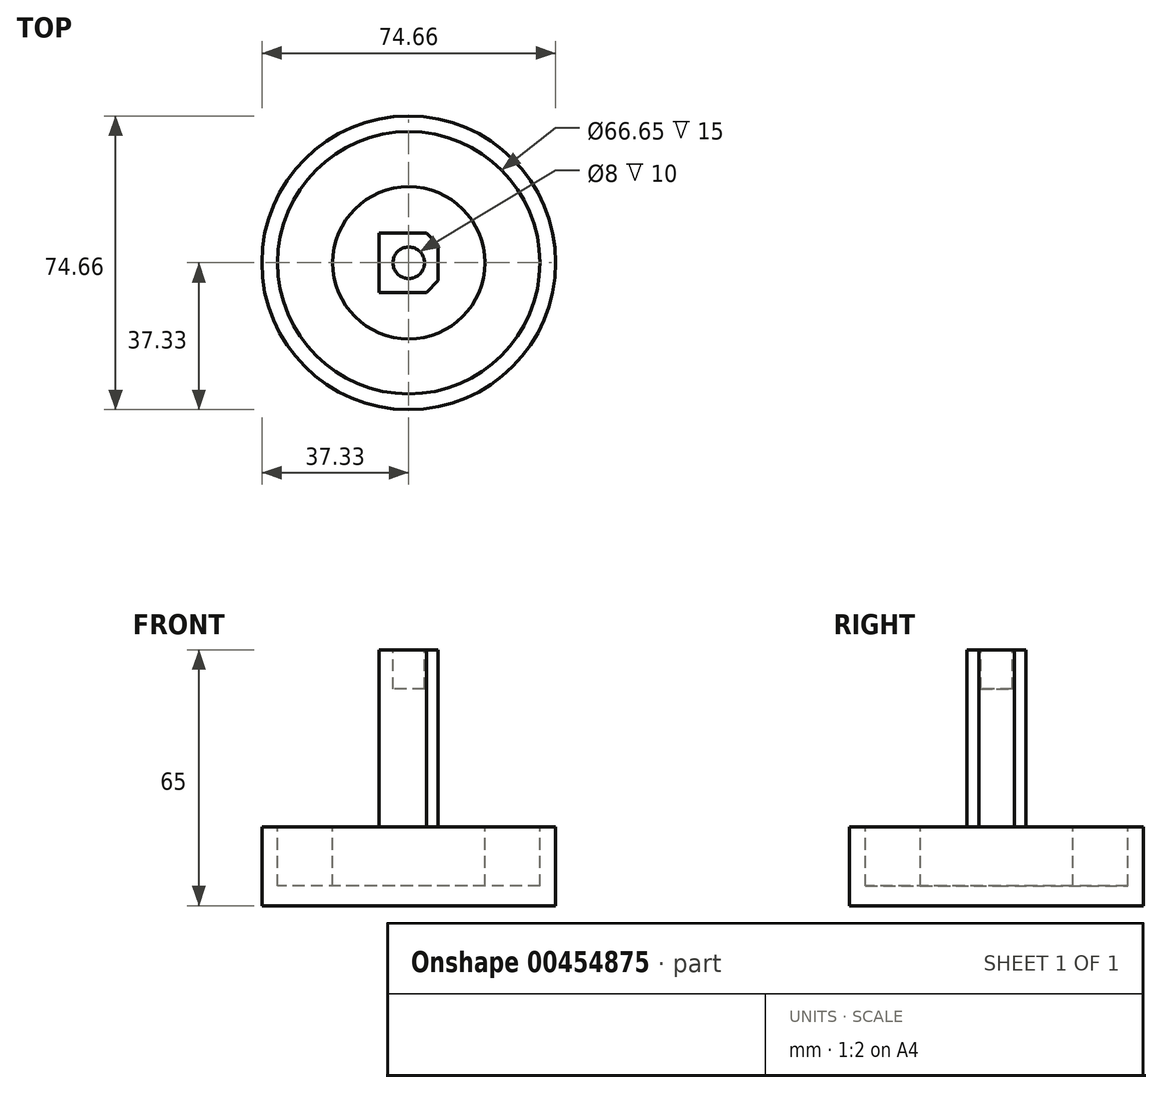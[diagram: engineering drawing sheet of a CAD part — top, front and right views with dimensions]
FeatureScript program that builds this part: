
annotation { "Feature Type Name" : "Feature", "Feature Type Description" : "" }
export const myFeature = defineFeature(function(context is Context, id is Id, definition is map)
    precondition{}
    {
        {
            var Q0;
            Q0=qCreatedBy(makeId("Top.planeOp"),FACE);
            var sketch = newSketch(context, id + "F0", { "sketchPlane" : qUnion([Q0])});
            skCircle(sketch, "E0", {"center": v(0, 0) * mm, "radius": 37.33 * mm});
            skSolve(sketch);
        }
        {
            var Q0;
            Q0=makeQuery(id+"F0.imprint","IMPRINT",FACE,{"disambiguationData":[TD([[makeQuery(id+"F0.imprint","IMPRINT",EDGE,{"derivedFrom":sQuery(id+"F0.wireOp",EDGE,"E0")}),1.0]])]});
            extrude(context, id + "F1", {"entities" : qUnion([Q0]), "depth" : 20 * mm});
        }
        {
            var Q0;
            Q0=makeQuery(id+"F1.opExtrude","CAP_FACE",FACE,{"disambiguationData":[OSD([sQuery(id+"F0.wireOp",EDGE,"E0")])],"isStart":false});
            var sketch = newSketch(context, id + "F2", { "sketchPlane" : qUnion([Q0])});
            skCircle(sketch, "E1.0", {"center": v(0, 0) * mm, "radius": 33.33 * mm});
            skCircle(sketch, "E2.0", {"center": v(0, 0) * mm, "radius": 19.33 * mm});
            skSolve(sketch);
        }
        {
            var Q0;
            Q0=makeQuery(id+"F2.imprint","IMPRINT",FACE,{"disambiguationData":[TD([[makeQuery(id+"F2.imprint","IMPRINT",EDGE,{"derivedFrom":sQuery(id+"F2.wireOp",EDGE,"E1.0")}),1.0]])]});
            extrude(context, id + "F3", {"entities" : qUnion([Q0]), "operationType" : NewBodyOperationType.REMOVE, "oppositeDirection" : true, "depth" : 15 * mm});
        }
        {
            var Q0;
            Q0=makeQuery(id+"F3.boolean.opBoolean","SPLIT",FACE,{"disambiguationData":[TD([makeQuery(id+"F3.opExtrude","SWEPT_FACE",FACE,{"disambiguationData":[OSD([sQuery(id+"F2.wireOp",EDGE,"E2.0")])]})])],"derivedFrom":makeQuery(id+"F1.opExtrude","CAP_FACE",FACE,{"disambiguationData":[OSD([sQuery(id+"F0.wireOp",EDGE,"E0")])],"isStart":false})});
            var sketch = newSketch(context, id + "F4", { "sketchPlane" : qUnion([Q0])});
            skLineSegment(sketch, "E3.bottom", {"start": v(7.5, 7.5) * mm, "end": v(-7.5, 7.5) * mm});
            skLineSegment(sketch, "E3.top", {"start": v(7.5, -7.5) * mm, "end": v(-7.5, -7.5) * mm});
            skLineSegment(sketch, "E3.left", {"start": v(7.5, 7.5) * mm, "end": v(7.5, -7.5) * mm});
            skLineSegment(sketch, "E3.right", {"start": v(-7.5, 7.5) * mm, "end": v(-7.5, -7.5) * mm});
            skPoint(sketch, "E3.middle", {"position": v(0, 0) * mm});
            skSolve(sketch);
        }
        {
            var Q0;
            Q0=makeQuery(id+"F4.imprint","IMPRINT",FACE,{"disambiguationData":[TD([[makeQuery(id+"F4.imprint","IMPRINT",EDGE,{"derivedFrom":sQuery(id+"F4.wireOp",EDGE,"E3.bottom")}),1.0]])]});
            extrude(context, id + "F5", {"entities" : qUnion([Q0]), "operationType" : NewBodyOperationType.ADD, "depth" : 45 * mm});
        }
        {
            var Q0;
            Q0=makeQuery(id+"F5.opExtrude","SWEPT_EDGE",EDGE,{"disambiguationData":[OSD([sQuery(id+"F4.wireOp",EDGE,"E3.bottom"),sQuery(id+"F4.wireOp",EDGE,"E3.left")])]});
            var Q1;
            Q1=makeQuery(id+"F5.opExtrude","SWEPT_EDGE",EDGE,{"disambiguationData":[OSD([sQuery(id+"F4.wireOp",EDGE,"E3.top"),sQuery(id+"F4.wireOp",EDGE,"E3.left")])]});
            chamfer(context, id + "F6", {"entities" : qUnion([Q0, Q1]), "chamferType" : ChamferType.OFFSET_ANGLE, "width" : 3 * mm, "oppositeDirection" : false, "angle" : 45 * degree, "tangentPropagation" : true});
        }
        {
            var Q0;
            Q0=makeQuery(id+"F5.opExtrude","CAP_FACE",FACE,{"disambiguationData":[OSD([sQuery(id+"F4.wireOp",EDGE,"E3.bottom"),sQuery(id+"F4.wireOp",EDGE,"E3.top"),sQuery(id+"F4.wireOp",EDGE,"E3.left"),sQuery(id+"F4.wireOp",EDGE,"E3.right")])],"isStart":false});
            var sketch = newSketch(context, id + "F7", { "sketchPlane" : qUnion([Q0])});
            skCircle(sketch, "E4", {"center": v(0, 0) * mm, "radius": 4 * mm});
            skSolve(sketch);
        }
        {
            var Q0;
            Q0=makeQuery(id+"F7.imprint","IMPRINT",FACE,{"disambiguationData":[TD([[makeQuery(id+"F7.imprint","IMPRINT",EDGE,{"derivedFrom":sQuery(id+"F7.wireOp",EDGE,"E4")}),1.0]])]});
            extrude(context, id + "F8", {"entities" : qUnion([Q0]), "operationType" : NewBodyOperationType.REMOVE, "oppositeDirection" : true, "depth" : 10 * mm});
        }
    });
